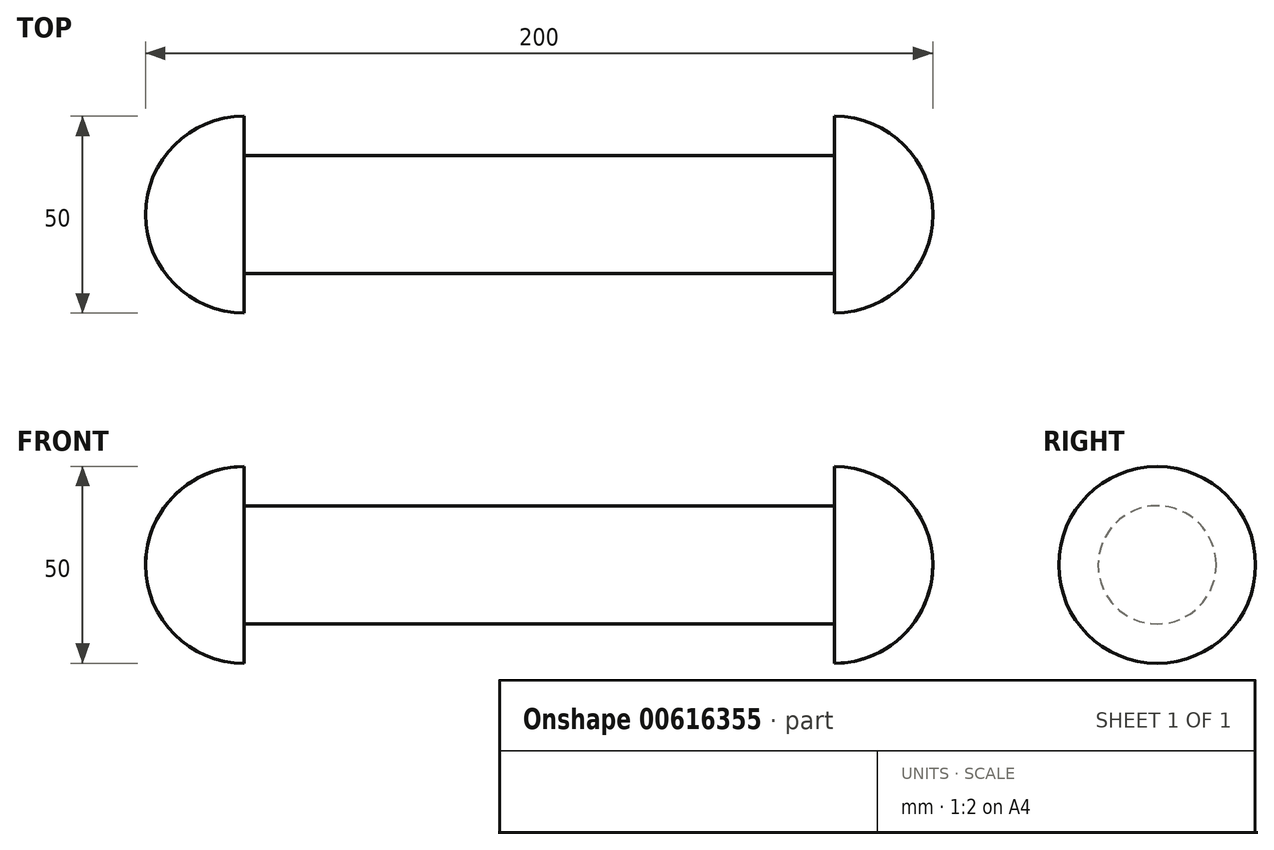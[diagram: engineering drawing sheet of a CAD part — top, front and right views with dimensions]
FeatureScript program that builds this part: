
annotation { "Feature Type Name" : "Feature", "Feature Type Description" : "" }
export const myFeature = defineFeature(function(context is Context, id is Id, definition is map)
    precondition{}
    {
        {
            var Q0;
            Q0=qCreatedBy(makeId("Front.planeOp"),FACE);
            var sketch = newSketch(context, id + "F0", { "sketchPlane" : qUnion([Q0])});
            skLineSegment(sketch, "E0", {"start": v(0, 0) * mm, "end": v(-75, 0) * mm});
            skLineSegment(sketch, "E1", {"start": v(-75, 15) * mm, "end": v(0, 15) * mm});
            skArc(sketch, "E2", {"start": v(25, 0) * mm, "mid": v(17.68, 17.68) * mm, "end": v(0, 25) * mm});
            skLineSegment(sketch, "E3", {"start": v(0, 0) * mm, "end": v(25, 0) * mm});
            skLineSegment(sketch, "E4", {"start": v(0, 15) * mm, "end": v(0, 25) * mm});
            skLineSegment(sketch, "E5", {"start": v(-75, 15) * mm, "end": v(-75, 0) * mm, "construction": true});
            skLineSegment(sketch, "E6.MirrorCS", {"start": v(-75, 15) * mm, "end": v(-150, 15) * mm});
            skLineSegment(sketch, "E7.MirrorCS", {"start": v(-150, 0) * mm, "end": v(-75, 0) * mm});
            skLineSegment(sketch, "E8.MirrorCS", {"start": v(-150, 0) * mm, "end": v(-175, 0) * mm});
            skArc(sketch, "E9.MirrorCS", {"start": v(-175, 0) * mm, "mid": v(-167.68, 17.68) * mm, "end": v(-150, 25) * mm});
            skLineSegment(sketch, "E10.MirrorCS", {"start": v(-150, 15) * mm, "end": v(-150, 25) * mm});
            skSolve(sketch);
        }
        {
            var Q0;
            Q0 = qSketchRegion(id + "F0", true);
            var Q1;
            Q1=sQuery(id+"F0.wireOp",EDGE,"E7.MirrorCS");
            revolve(context, id + "F1", {"entities" : qUnion([Q0]), "axis" : qUnion([Q1]), "revolveType" : RevolveType.FULL});
        }
    });
